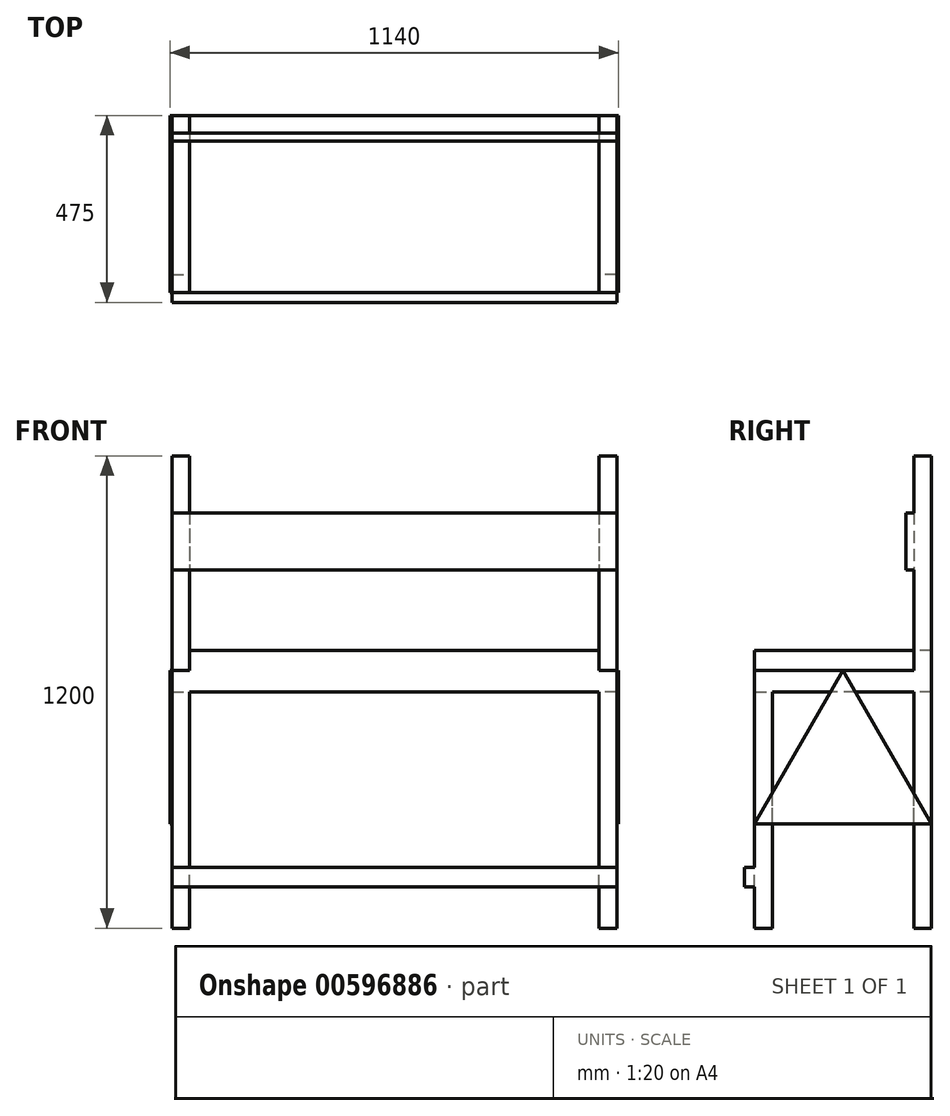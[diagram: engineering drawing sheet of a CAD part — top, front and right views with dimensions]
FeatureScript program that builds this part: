
annotation { "Feature Type Name" : "Feature", "Feature Type Description" : "" }
export const myFeature = defineFeature(function(context is Context, id is Id, definition is map)
    precondition{}
    {
        {
            var Q0;
            Q0=qCreatedBy(makeId("Top.planeOp"),FACE);
            var sketch = newSketch(context, id + "F0", { "sketchPlane" : qUnion([Q0])});
            skLineSegment(sketch, "E0.bottom", {"start": v(-575.88, 97.03) * mm, "end": v(554.12, 97.03) * mm});
            skLineSegment(sketch, "E0.top", {"start": v(-575.88, -352.97) * mm, "end": v(554.12, -352.97) * mm});
            skLineSegment(sketch, "E0.left", {"start": v(-575.88, 97.03) * mm, "end": v(-575.88, -352.97) * mm});
            skLineSegment(sketch, "E0.right", {"start": v(554.12, 97.03) * mm, "end": v(554.12, -352.97) * mm});
            skSolve(sketch);
        }
        {
            var Q0;
            Q0=makeQuery(id+"F0.imprint","IMPRINT",FACE,{"disambiguationData":[TD([[makeQuery(id+"F0.imprint","IMPRINT",EDGE,{"derivedFrom":sQuery(id+"F0.wireOp",EDGE,"E0.bottom")}),-1.0]])]});
            extrude(context, id + "F1", {"entities" : qUnion([Q0]), "depth" : 55 * mm, "offsetDistance" : 25 * mm});
        }
        {
            var Q0;
            Q0=makeQuery(id+"F1.opExtrude","CAP_FACE",FACE,{"disambiguationData":[OSD([sQuery(id+"F0.wireOp",EDGE,"E0.bottom"),sQuery(id+"F0.wireOp",EDGE,"E0.top"),sQuery(id+"F0.wireOp",EDGE,"E0.left"),sQuery(id+"F0.wireOp",EDGE,"E0.right")])],"isStart":true});
            var sketch = newSketch(context, id + "F2", { "sketchPlane" : qUnion([Q0])});
            skLineSegment(sketch, "E1.bottom", {"start": v(554.12, -97.03) * mm, "end": v(509.12, -97.03) * mm});
            skLineSegment(sketch, "E1.top", {"start": v(554.12, -52.03) * mm, "end": v(509.12, -52.03) * mm});
            skLineSegment(sketch, "E1.left", {"start": v(554.12, -97.03) * mm, "end": v(554.12, -52.03) * mm});
            skLineSegment(sketch, "E1.right", {"start": v(509.12, -97.03) * mm, "end": v(509.12, -52.03) * mm});
            skSolve(sketch);
        }
        {
            var Q0;
            Q0 = qSketchRegion(id + "F2", true);
            extrude(context, id + "F3", {"entities" : qUnion([Q0]), "operationType" : NewBodyOperationType.ADD, "depth" : 600 * mm, "offsetDistance" : 25 * mm});
        }
        {
            var Q0;
            Q0=makeQuery(id+"F1.opExtrude","CAP_FACE",FACE,{"disambiguationData":[OSD([sQuery(id+"F0.wireOp",EDGE,"E0.bottom"),sQuery(id+"F0.wireOp",EDGE,"E0.top"),sQuery(id+"F0.wireOp",EDGE,"E0.left"),sQuery(id+"F0.wireOp",EDGE,"E0.right")])],"isStart":true});
            var sketch = newSketch(context, id + "F4", { "sketchPlane" : qUnion([Q0])});
            skLineSegment(sketch, "E2.bottom", {"start": v(-575.88, -97.03) * mm, "end": v(-530.88, -97.03) * mm});
            skLineSegment(sketch, "E2.top", {"start": v(-575.88, -52.03) * mm, "end": v(-530.88, -52.03) * mm});
            skLineSegment(sketch, "E2.left", {"start": v(-575.88, -97.03) * mm, "end": v(-575.88, -52.03) * mm});
            skLineSegment(sketch, "E2.right", {"start": v(-530.88, -97.03) * mm, "end": v(-530.88, -52.03) * mm});
            skSolve(sketch);
        }
        {
            var Q0;
            Q0 = qSketchRegion(id + "F4", true);
            extrude(context, id + "F5", {"entities" : qUnion([Q0]), "operationType" : NewBodyOperationType.ADD, "depth" : 600 * mm, "offsetDistance" : 25 * mm});
        }
        {
            var Q0;
            Q0=makeQuery(id+"F1.opExtrude","CAP_FACE",FACE,{"disambiguationData":[OSD([sQuery(id+"F0.wireOp",EDGE,"E0.bottom"),sQuery(id+"F0.wireOp",EDGE,"E0.top"),sQuery(id+"F0.wireOp",EDGE,"E0.left"),sQuery(id+"F0.wireOp",EDGE,"E0.right")])],"isStart":true});
            var sketch = newSketch(context, id + "F6", { "sketchPlane" : qUnion([Q0])});
            skLineSegment(sketch, "E3.bottom", {"start": v(554.12, 352.97) * mm, "end": v(509.12, 352.97) * mm});
            skLineSegment(sketch, "E3.top", {"start": v(554.12, 307.97) * mm, "end": v(509.12, 307.97) * mm});
            skLineSegment(sketch, "E3.left", {"start": v(554.12, 352.97) * mm, "end": v(554.12, 307.97) * mm});
            skLineSegment(sketch, "E3.right", {"start": v(509.12, 352.97) * mm, "end": v(509.12, 307.97) * mm});
            skSolve(sketch);
        }
        {
            var Q0;
            Q0 = qSketchRegion(id + "F6", true);
            extrude(context, id + "F7", {"entities" : qUnion([Q0]), "operationType" : NewBodyOperationType.ADD, "depth" : 600 * mm, "offsetDistance" : 25 * mm});
        }
        {
            var Q0;
            Q0=makeQuery(id+"F1.opExtrude","CAP_FACE",FACE,{"disambiguationData":[OSD([sQuery(id+"F0.wireOp",EDGE,"E0.bottom"),sQuery(id+"F0.wireOp",EDGE,"E0.top"),sQuery(id+"F0.wireOp",EDGE,"E0.left"),sQuery(id+"F0.wireOp",EDGE,"E0.right")])],"isStart":true});
            var sketch = newSketch(context, id + "F8", { "sketchPlane" : qUnion([Q0])});
            skLineSegment(sketch, "E4.bottom", {"start": v(-575.88, 352.97) * mm, "end": v(-530.88, 352.97) * mm});
            skLineSegment(sketch, "E4.top", {"start": v(-575.88, 307.97) * mm, "end": v(-530.88, 307.97) * mm});
            skLineSegment(sketch, "E4.left", {"start": v(-575.88, 352.97) * mm, "end": v(-575.88, 307.97) * mm});
            skLineSegment(sketch, "E4.right", {"start": v(-530.88, 352.97) * mm, "end": v(-530.88, 307.97) * mm});
            skSolve(sketch);
        }
        {
            var Q0;
            Q0=makeQuery(id+"F8.imprint","IMPRINT",FACE,{"disambiguationData":[TD([[makeQuery(id+"F8.imprint","IMPRINT",EDGE,{"derivedFrom":sQuery(id+"F8.wireOp",EDGE,"E4.bottom")}),-1.0]])]});
            extrude(context, id + "F9", {"entities" : qUnion([Q0]), "operationType" : NewBodyOperationType.ADD, "depth" : 600 * mm, "offsetDistance" : 25 * mm});
        }
        {
            var Q0;
            Q0=makeQuery(id+"F1.opExtrude","CAP_FACE",FACE,{"disambiguationData":[OSD([sQuery(id+"F0.wireOp",EDGE,"E0.bottom"),sQuery(id+"F0.wireOp",EDGE,"E0.top"),sQuery(id+"F0.wireOp",EDGE,"E0.left"),sQuery(id+"F0.wireOp",EDGE,"E0.right")])],"isStart":false});
            var sketch = newSketch(context, id + "F10", { "sketchPlane" : qUnion([Q0])});
            skLineSegment(sketch, "E5.bottom", {"start": v(554.12, 97.03) * mm, "end": v(509.12, 97.03) * mm});
            skLineSegment(sketch, "E5.top", {"start": v(554.12, 52.03) * mm, "end": v(509.12, 52.03) * mm});
            skLineSegment(sketch, "E5.left", {"start": v(554.12, 97.03) * mm, "end": v(554.12, 52.03) * mm});
            skLineSegment(sketch, "E5.right", {"start": v(509.12, 97.03) * mm, "end": v(509.12, 52.03) * mm});
            skSolve(sketch);
        }
        {
            var Q0;
            Q0 = qSketchRegion(id + "F10", true);
            extrude(context, id + "F11", {"entities" : qUnion([Q0]), "operationType" : NewBodyOperationType.ADD, "depth" : 545 * mm, "offsetDistance" : 25 * mm});
        }
        {
            var Q0;
            Q0=makeQuery(id+"F1.opExtrude","CAP_FACE",FACE,{"disambiguationData":[OSD([sQuery(id+"F0.wireOp",EDGE,"E0.bottom"),sQuery(id+"F0.wireOp",EDGE,"E0.top"),sQuery(id+"F0.wireOp",EDGE,"E0.left"),sQuery(id+"F0.wireOp",EDGE,"E0.right")])],"isStart":false});
            var sketch = newSketch(context, id + "F12", { "sketchPlane" : qUnion([Q0])});
            skLineSegment(sketch, "E6.bottom", {"start": v(-575.88, 97.03) * mm, "end": v(-530.88, 97.03) * mm});
            skLineSegment(sketch, "E6.top", {"start": v(-575.88, 52.03) * mm, "end": v(-530.88, 52.03) * mm});
            skLineSegment(sketch, "E6.left", {"start": v(-575.88, 97.03) * mm, "end": v(-575.88, 52.03) * mm});
            skLineSegment(sketch, "E6.right", {"start": v(-530.88, 97.03) * mm, "end": v(-530.88, 52.03) * mm});
            skSolve(sketch);
        }
        {
            var Q0;
            Q0 = qSketchRegion(id + "F12", true);
            extrude(context, id + "F13", {"entities" : qUnion([Q0]), "operationType" : NewBodyOperationType.ADD, "depth" : 545 * mm, "offsetDistance" : 25 * mm});
        }
        {
            var Q0;
            Q0=makeQuery(id+"F11.opExtrude","SWEPT_FACE",FACE,{"disambiguationData":[OSD([sQuery(id+"F10.wireOp",EDGE,"E5.top")])]});
            var sketch = newSketch(context, id + "F14", { "sketchPlane" : qUnion([Q0])});
            skLineSegment(sketch, "E7.top", {"start": v(554.12, 310) * mm, "end": v(-575.88, 310) * mm});
            skLineSegment(sketch, "E7.left", {"start": v(554.12, 455) * mm, "end": v(554.12, 310) * mm});
            skLineSegment(sketch, "E7.right", {"start": v(-575.88, 455) * mm, "end": v(-575.88, 310) * mm});
            skLineSegment(sketch, "E8", {"start": v(-575.88, 455) * mm, "end": v(554.12, 455) * mm});
            skPoint(sketch, "E7.bottom.start.orphan", {"position": v(554.12, 600) * mm});
            skPoint(sketch, "E9.orphan", {"position": v(-575.88, 600) * mm});
            skSolve(sketch);
        }
        {
            var Q0;
            Q0 = qSketchRegion(id + "F14", true);
            extrude(context, id + "F15", {"entities" : qUnion([Q0]), "operationType" : NewBodyOperationType.ADD, "depth" : 20 * mm, "offsetDistance" : 25 * mm});
        }
        {
            var Q0;
            Q0=makeQuery(id+"F9.boolean.opBoolean","MERGE",FACE,{"derivedFrom":[makeQuery(id+"F7.boolean.opBoolean","MERGE",FACE,{"derivedFrom":[makeQuery(id+"F1.opExtrude","SWEPT_FACE",FACE,{"disambiguationData":[OSD([sQuery(id+"F0.wireOp",EDGE,"E0.top")])]}),makeQuery(id+"F7.opExtrude","SWEPT_FACE",FACE,{"disambiguationData":[OSD([sQuery(id+"F6.wireOp",EDGE,"E3.bottom")])]})]}),makeQuery(id+"F9.opExtrude","SWEPT_FACE",FACE,{"disambiguationData":[OSD([sQuery(id+"F8.wireOp",EDGE,"E4.bottom")])]})]});
            var sketch = newSketch(context, id + "F16", { "sketchPlane" : qUnion([Q0])});
            skLineSegment(sketch, "E10.top", {"start": v(554.12, -445.05) * mm, "end": v(-575.88, -445.05) * mm});
            skLineSegment(sketch, "E11.bottom", {"start": v(-575.88, -445.05) * mm, "end": v(554.12, -445.05) * mm});
            skLineSegment(sketch, "E11.top", {"start": v(-575.88, -495.05) * mm, "end": v(554.12, -495.05) * mm});
            skLineSegment(sketch, "E11.left", {"start": v(-575.88, -445.05) * mm, "end": v(-575.88, -495.05) * mm});
            skLineSegment(sketch, "E11.right", {"start": v(554.12, -445.05) * mm, "end": v(554.12, -495.05) * mm});
            skSolve(sketch);
        }
        {
            var Q0;
            Q0 = qSketchRegion(id + "F16", true);
            extrude(context, id + "F17", {"entities" : qUnion([Q0]), "operationType" : NewBodyOperationType.ADD, "depth" : 25 * mm, "offsetDistance" : 25 * mm});
        }
        {
            var Q0;
            Q0=makeQuery(id+"F1.opExtrude","CAP_FACE",FACE,{"disambiguationData":[OSD([sQuery(id+"F0.wireOp",EDGE,"E0.bottom"),sQuery(id+"F0.wireOp",EDGE,"E0.top"),sQuery(id+"F0.wireOp",EDGE,"E0.left"),sQuery(id+"F0.wireOp",EDGE,"E0.right")])],"isStart":false});
            var sketch = newSketch(context, id + "F18", { "sketchPlane" : qUnion([Q0])});
            skLineSegment(sketch, "E12.bottom", {"start": v(-530.88, 97.03) * mm, "end": v(509.12, 97.03) * mm});
            skLineSegment(sketch, "E12.top", {"start": v(-530.88, -352.97) * mm, "end": v(509.12, -352.97) * mm});
            skLineSegment(sketch, "E12.left", {"start": v(-530.88, 97.03) * mm, "end": v(-530.88, -352.97) * mm});
            skLineSegment(sketch, "E12.right", {"start": v(509.12, 97.03) * mm, "end": v(509.12, -352.97) * mm});
            skSolve(sketch);
        }
        {
            var Q0;
            Q0 = qSketchRegion(id + "F18", true);
            extrude(context, id + "F19", {"entities" : qUnion([Q0]), "operationType" : NewBodyOperationType.ADD, "depth" : 50 * mm, "offsetDistance" : 25 * mm});
        }
        {
            var Q0;
            Q0=makeQuery(id+"F17.boolean.opBoolean","MERGE",FACE,{"derivedFrom":[makeQuery(id+"F15.boolean.opBoolean","MERGE",FACE,{"derivedFrom":[makeQuery(id+"F11.boolean.opBoolean","MERGE",FACE,{"derivedFrom":[makeQuery(id+"F7.boolean.opBoolean","MERGE",FACE,{"derivedFrom":[makeQuery(id+"F3.boolean.opBoolean","MERGE",FACE,{"derivedFrom":[makeQuery(id+"F1.opExtrude","SWEPT_FACE",FACE,{"disambiguationData":[OSD([sQuery(id+"F0.wireOp",EDGE,"E0.right")])]}),makeQuery(id+"F3.opExtrude","SWEPT_FACE",FACE,{"disambiguationData":[OSD([sQuery(id+"F2.wireOp",EDGE,"E1.left")])]})]}),makeQuery(id+"F7.opExtrude","SWEPT_FACE",FACE,{"disambiguationData":[OSD([sQuery(id+"F6.wireOp",EDGE,"E3.left")])]})]}),makeQuery(id+"F11.opExtrude","SWEPT_FACE",FACE,{"disambiguationData":[OSD([sQuery(id+"F10.wireOp",EDGE,"E5.left")])]})]}),makeQuery(id+"F15.opExtrude","SWEPT_FACE",FACE,{"disambiguationData":[OSD([sQuery(id+"F14.wireOp",EDGE,"E7.left")])]})]}),makeQuery(id+"F17.opExtrude","SWEPT_FACE",FACE,{"disambiguationData":[OSD([sQuery(id+"F16.wireOp",EDGE,"E11.right")])]})]});
            var sketch = newSketch(context, id + "F20", { "sketchPlane" : qUnion([Q0])});
            skLineSegment(sketch, "E13.top", {"start": v(-352.97, -335) * mm, "end": v(97.03, -335) * mm});
            skLineSegment(sketch, "E14", {"start": v(-127.97, 55) * mm, "end": v(97.03, -335) * mm});
            skLineSegment(sketch, "E15", {"start": v(-352.97, -335) * mm, "end": v(-127.97, 55) * mm});
            skPoint(sketch, "E13.right.start.orphan", {"position": v(97.03, 55) * mm});
            skPoint(sketch, "E16.start.orphan", {"position": v(-352.97, 55) * mm});
            skSolve(sketch);
        }
        {
            var Q0;
            Q0 = qSketchRegion(id + "F20", true);
            extrude(context, id + "F21", {"entities" : qUnion([Q0]), "operationType" : NewBodyOperationType.ADD, "depth" : 5 * mm, "offsetDistance" : 25 * mm});
        }
        {
            var Q0;
            Q0=makeQuery(id+"F17.boolean.opBoolean","MERGE",FACE,{"derivedFrom":[makeQuery(id+"F15.boolean.opBoolean","MERGE",FACE,{"derivedFrom":[makeQuery(id+"F13.boolean.opBoolean","MERGE",FACE,{"derivedFrom":[makeQuery(id+"F9.boolean.opBoolean","MERGE",FACE,{"derivedFrom":[makeQuery(id+"F5.boolean.opBoolean","MERGE",FACE,{"derivedFrom":[makeQuery(id+"F1.opExtrude","SWEPT_FACE",FACE,{"disambiguationData":[OSD([sQuery(id+"F0.wireOp",EDGE,"E0.left")])]}),makeQuery(id+"F5.opExtrude","SWEPT_FACE",FACE,{"disambiguationData":[OSD([sQuery(id+"F4.wireOp",EDGE,"E2.left")])]})]}),makeQuery(id+"F9.opExtrude","SWEPT_FACE",FACE,{"disambiguationData":[OSD([sQuery(id+"F8.wireOp",EDGE,"E4.left")])]})]}),makeQuery(id+"F13.opExtrude","SWEPT_FACE",FACE,{"disambiguationData":[OSD([sQuery(id+"F12.wireOp",EDGE,"E6.left")])]})]}),makeQuery(id+"F15.opExtrude","SWEPT_FACE",FACE,{"disambiguationData":[OSD([sQuery(id+"F14.wireOp",EDGE,"E7.right")])]})]}),makeQuery(id+"F17.opExtrude","SWEPT_FACE",FACE,{"disambiguationData":[OSD([sQuery(id+"F16.wireOp",EDGE,"E11.left")])]})]});
            var sketch = newSketch(context, id + "F22", { "sketchPlane" : qUnion([Q0])});
            skPoint(sketch, "E17.bottom.end.orphan", {"position": v(127.97, 0) * mm});
            skPoint(sketch, "E17.right.start.orphan", {"position": v(352.97, 0) * mm});
            skPoint(sketch, "E17.left.start.orphan", {"position": v(-97.03, 0) * mm});
            skLineSegment(sketch, "E18.top", {"start": v(352.97, -335) * mm, "end": v(-97.03, -335) * mm});
            skLineSegment(sketch, "E19", {"start": v(127.97, 55) * mm, "end": v(352.97, -335) * mm});
            skLineSegment(sketch, "E20", {"start": v(-97.03, -335) * mm, "end": v(127.97, 55) * mm});
            skPoint(sketch, "E18.left.start.orphan", {"position": v(352.97, 55) * mm});
            skPoint(sketch, "E18.right.start.orphan", {"position": v(-97.03, 55) * mm});
            skSolve(sketch);
        }
        {
            var Q0;
            Q0 = qSketchRegion(id + "F22", true);
            extrude(context, id + "F23", {"entities" : qUnion([Q0]), "operationType" : NewBodyOperationType.ADD, "depth" : 5 * mm, "offsetDistance" : 25 * mm});
        }
    });
